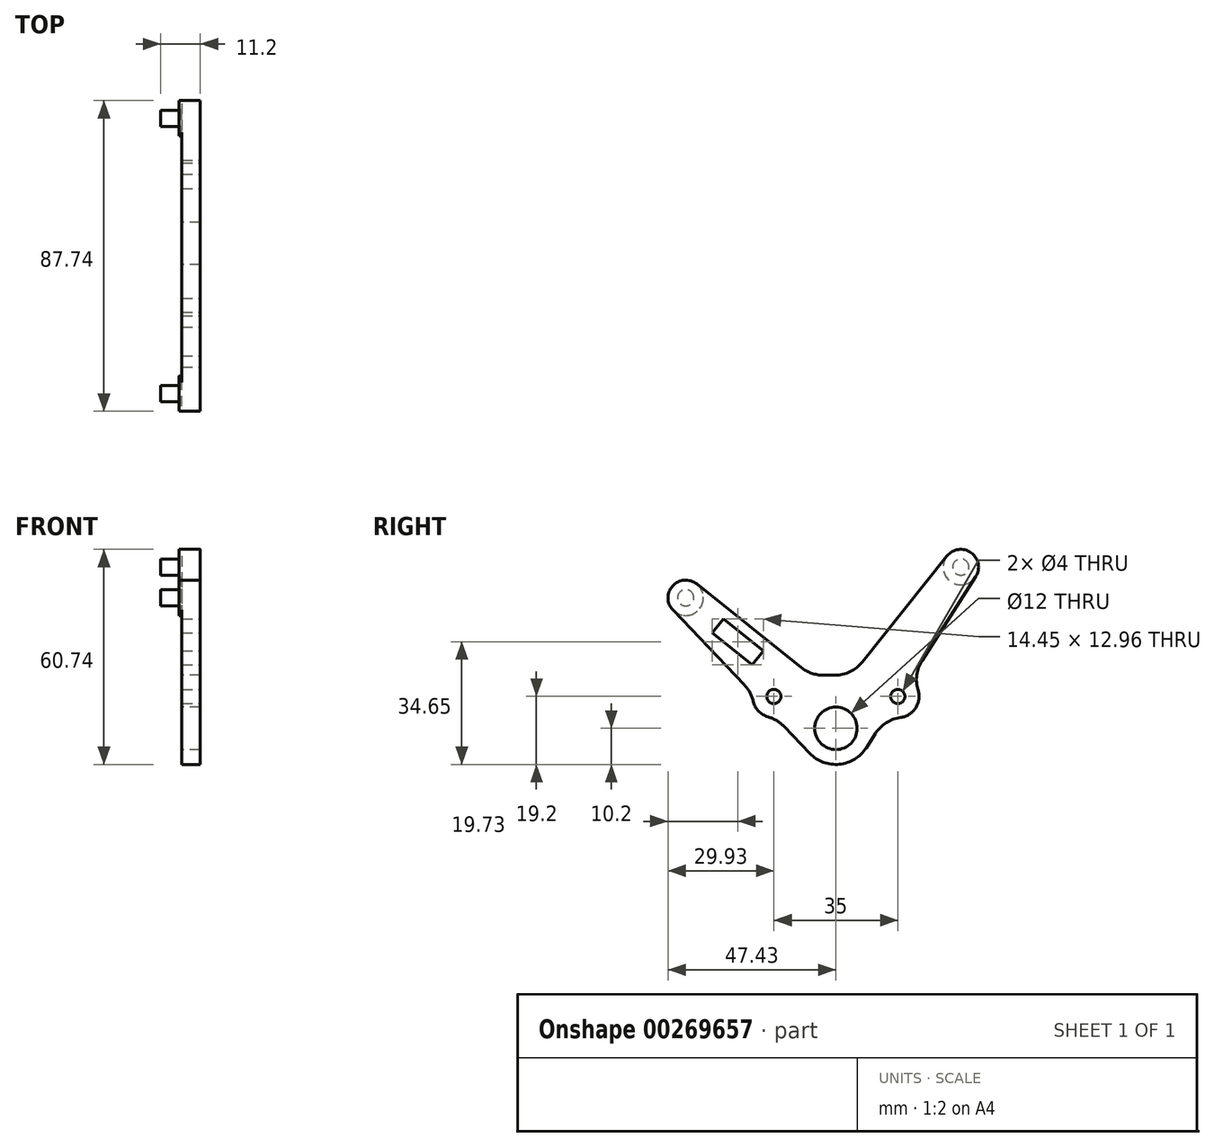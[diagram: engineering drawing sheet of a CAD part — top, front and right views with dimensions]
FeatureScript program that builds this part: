
annotation { "Feature Type Name" : "Feature", "Feature Type Description" : "" }
export const myFeature = defineFeature(function(context is Context, id is Id, definition is map)
    precondition{}
    {
        {
            var Q0;
            Q0=qCreatedBy(makeId("Right.planeOp"),FACE);
            var sketch = newSketch(context, id + "F0", { "sketchPlane" : qUnion([Q0])});
            skArc(sketch, "E0", {"start": v(-7.37, -7.05) * mm, "mid": v(0.99, -10.15) * mm, "end": v(8.6, -5.5) * mm});
            skLineSegment(sketch, "E1", {"start": v(39.52, 42.85) * mm, "end": v(8.6, -5.5) * mm});
            skLineSegment(sketch, "E2", {"start": v(-46.04, 33.4) * mm, "end": v(-7.37, -7.05) * mm});
            skCircle(sketch, "E3", {"center": v(0, 0) * mm, "radius": 6 * mm});
            skLineSegment(sketch, "E4", {"start": v(31.4, 48.66) * mm, "end": v(0, 9.36) * mm});
            skLineSegment(sketch, "E5", {"start": v(0, 9.36) * mm, "end": v(-39.3, 40.76) * mm});
            skArc(sketch, "E6", {"start": v(39.52, 42.85) * mm, "mid": v(38.22, 49.6) * mm, "end": v(31.4, 48.66) * mm});
            skArc(sketch, "E7", {"start": v(-39.3, 40.76) * mm, "mid": v(-46.12, 40.23) * mm, "end": v(-46.04, 33.4) * mm});
            skLineSegment(sketch, "E8", {"start": v(35.31, 45.54) * mm, "end": v(-42.43, 36.86) * mm, "construction": true});
            skSolve(sketch);
        }
        {
            var Q0;
            Q0 = qSketchRegion(id + "F0", true);
            extrude(context, id + "F1", {"entities" : qUnion([Q0]), "depth" : 5.2 * mm});
        }
        {
            var Q0;
            Q0=makeQuery(id+"F1.opExtrude","CAP_FACE",FACE,{"disambiguationData":[OSD([sQuery(id+"F0.wireOp",EDGE,"E0"),sQuery(id+"F0.wireOp",EDGE,"E1"),sQuery(id+"F0.wireOp",EDGE,"E2"),sQuery(id+"F0.wireOp",EDGE,"E3"),sQuery(id+"F0.wireOp",EDGE,"6CrYnnp3-bjRy-a3A9-He7e-rV40i75ghI31.top"),sQuery(id+"F0.wireOp",EDGE,"6CrYnnp3-bjRy-a3A9-He7e-rV40i75ghI31.left"),sQuery(id+"F0.wireOp",EDGE,"6CrYnnp3-bjRy-a3A9-He7e-rV40i75ghI31.right")])],"isStart":false});
            var sketch = newSketch(context, id + "F2", { "sketchPlane" : qUnion([Q0])});
            skLineSegment(sketch, "E9", {"start": v(17.5, 3) * mm, "end": v(5.2, 3) * mm});
            skArc(sketch, "E10", {"start": v(17.5, 3) * mm, "mid": v(23.5, 9) * mm, "end": v(17.5, 15) * mm});
            skLineSegment(sketch, "E11", {"start": v(0, 0) * mm, "end": v(0, 22.38) * mm, "construction": true});
            skLineSegment(sketch, "E12.trimOffspring", {"start": v(-5.2, 3) * mm, "end": v(-17.5, 3) * mm});
            skLineSegment(sketch, "E13", {"start": v(17.5, 9) * mm, "end": v(-17.5, 9) * mm, "construction": true});
            skArc(sketch, "E14.0", {"start": v(5.2, 3) * mm, "mid": v(0, 6) * mm, "end": v(-5.2, 3) * mm});
            skArc(sketch, "E15", {"start": v(-17.5, 15) * mm, "mid": v(-23.5, 9) * mm, "end": v(-17.5, 3) * mm});
            skLineSegment(sketch, "E16", {"start": v(17.5, 15) * mm, "end": v(-17.5, 15) * mm});
            skSolve(sketch);
        }
        {
            var Q0;
            Q0 = qSketchRegion(id + "F2", true);
            var Q1;
            Q1=makeQuery(id+"F1.opExtrude","CAP_FACE",FACE,{"disambiguationData":[OSD([sQuery(id+"F0.wireOp",EDGE,"E0"),sQuery(id+"F0.wireOp",EDGE,"E1"),sQuery(id+"F0.wireOp",EDGE,"E2"),sQuery(id+"F0.wireOp",EDGE,"E3"),sQuery(id+"F0.wireOp",EDGE,"6CrYnnp3-bjRy-a3A9-He7e-rV40i75ghI31.top"),sQuery(id+"F0.wireOp",EDGE,"6CrYnnp3-bjRy-a3A9-He7e-rV40i75ghI31.left"),sQuery(id+"F0.wireOp",EDGE,"6CrYnnp3-bjRy-a3A9-He7e-rV40i75ghI31.right")])],"isStart":true});
            extrude(context, id + "F3", {"entities" : qUnion([Q0]), "operationType" : NewBodyOperationType.ADD, "endBound" : BoundingType.UP_TO_SURFACE, "oppositeDirection" : true, "endBoundEntityFace" : qUnion([Q1]), "depth" : 25 * mm});
        }
        {
            var Q0;
            Q0=makeQuery(id+"F3.boolean.opBoolean","MERGE",FACE,{"derivedFrom":[makeQuery(id+"F1.opExtrude","CAP_FACE",FACE,{"disambiguationData":[OSD([sQuery(id+"F0.wireOp",EDGE,"E0"),sQuery(id+"F0.wireOp",EDGE,"E1"),sQuery(id+"F0.wireOp",EDGE,"E2"),sQuery(id+"F0.wireOp",EDGE,"E3"),sQuery(id+"F0.wireOp",EDGE,"6CrYnnp3-bjRy-a3A9-He7e-rV40i75ghI31.top"),sQuery(id+"F0.wireOp",EDGE,"6CrYnnp3-bjRy-a3A9-He7e-rV40i75ghI31.left"),sQuery(id+"F0.wireOp",EDGE,"6CrYnnp3-bjRy-a3A9-He7e-rV40i75ghI31.right")])],"isStart":false}),makeQuery(id+"F3.opExtrude","CAP_FACE",FACE,{"disambiguationData":[OSD([sQuery(id+"F2.wireOp",EDGE,"E9"),sQuery(id+"F2.wireOp",EDGE,"E10"),sQuery(id+"F2.wireOp",EDGE,"EYINIPp3-QXVF-pmR1-TqJy-1Ml2RVj9I1TC")])],"isStart":true}),makeQuery(id+"F3.opExtrude","CAP_FACE",FACE,{"disambiguationData":[OSD([sQuery(id+"F2.wireOp",EDGE,"iWNl47SU-lmgI-QhfJ-MTGu-GNKagXJEW7x7"),sQuery(id+"F2.wireOp",EDGE,"ciIXBD7B-xHR2-47Qe-O2mZ-nUJdmOusYSC5"),sQuery(id+"F2.wireOp",EDGE,"E12.trimOffspring")])],"isStart":true})]});
            var sketch = newSketch(context, id + "F4", { "sketchPlane" : qUnion([Q0])});
            skLineSegment(sketch, "E17", {"start": v(-17.5, 9) * mm, "end": v(17.5, 9) * mm, "construction": true});
            skLineSegment(sketch, "E18", {"start": v(0, 0.97) * mm, "end": v(0, 29.51) * mm, "construction": true});
            skCircle(sketch, "E19", {"center": v(-17.5, 9) * mm, "radius": 2 * mm});
            skCircle(sketch, "E20", {"center": v(17.5, 9) * mm, "radius": 2 * mm});
            skSolve(sketch);
        }
        {
            var Q0;
            Q0 = qSketchRegion(id + "F4", true);
            extrude(context, id + "F5", {"entities" : qUnion([Q0]), "operationType" : NewBodyOperationType.REMOVE, "endBound" : BoundingType.THROUGH_ALL, "oppositeDirection" : true, "depth" : 25 * mm});
        }
        {
            var Q0;
            {var subQ0=sQuery(id+"F0.wireOp",EDGE,"E7");var subQ1=sQuery(id+"F0.wireOp",EDGE,"E6");var subQ2=sQuery(id+"F0.wireOp",EDGE,"E5");var subQ3=sQuery(id+"F0.wireOp",EDGE,"E4");var subQ4=sQuery(id+"F0.wireOp",EDGE,"E3");var subQ5=sQuery(id+"F0.wireOp",EDGE,"E2");var subQ6=sQuery(id+"F0.wireOp",EDGE,"E1");var subQ7=sQuery(id+"F0.wireOp",EDGE,"E0");Q0=makeQuery(id+"F3.boolean.opBoolean","MERGE",FACE,{"derivedFrom":[makeQuery(id+"F1.opExtrude","CAP_FACE",FACE,{"disambiguationData":[OSD([subQ7,subQ6,subQ5,subQ4,subQ3,subQ2,subQ1,subQ0])],"isStart":true}),makeQuery(id+"F3.opExtrude","CAP_FACE",FACE,{"disambiguationData":[OSD([subQ7,subQ6,subQ5,subQ4,subQ3,subQ2,subQ1,subQ0]),ownerDisambiguation([makeQuery(id+"F3.opExtrude","SWEPT_BODY",BODY,{"disambiguationData":[OSD([sQuery(id+"F2.wireOp",EDGE,"E9"),sQuery(id+"F2.wireOp",EDGE,"E10"),sQuery(id+"F2.wireOp",EDGE,"EYINIPp3-QXVF-pmR1-TqJy-1Ml2RVj9I1TC")])]})])],"isStart":false}),makeQuery(id+"F3.opExtrude","CAP_FACE",FACE,{"disambiguationData":[OSD([subQ7,subQ6,subQ5,subQ4,subQ3,subQ2,subQ1,subQ0]),ownerDisambiguation([makeQuery(id+"F3.opExtrude","SWEPT_BODY",BODY,{"disambiguationData":[OSD([sQuery(id+"F2.wireOp",EDGE,"iWNl47SU-lmgI-QhfJ-MTGu-GNKagXJEW7x7"),sQuery(id+"F2.wireOp",EDGE,"ciIXBD7B-xHR2-47Qe-O2mZ-nUJdmOusYSC5"),sQuery(id+"F2.wireOp",EDGE,"E12.trimOffspring")])]})])],"isStart":false})]});}
            var sketch = newSketch(context, id + "F6", { "sketchPlane" : qUnion([Q0])});
            skCircle(sketch, "E21", {"center": v(-35.31, 45.54) * mm, "radius": 2.3 * mm});
            skCircle(sketch, "E22", {"center": v(42.43, 36.86) * mm, "radius": 2.3 * mm});
            skSolve(sketch);
        }
        {
            var Q0;
            Q0 = qSketchRegion(id + "F6", true);
            extrude(context, id + "F7", {"entities" : qUnion([Q0]), "operationType" : NewBodyOperationType.ADD, "depth" : 6 * mm});
        }
        {
            var Q0;
            Q0=makeQuery(id+"F3.boolean.opBoolean","INTERSECT",EDGE,{"derivedFrom":[makeQuery(id+"F1.opExtrude","SWEPT_FACE",FACE,{"disambiguationData":[OSD([sQuery(id+"F0.wireOp",EDGE,"E4")])]}),makeQuery(id+"F3.opExtrude","SWEPT_FACE",FACE,{"disambiguationData":[OSD([sQuery(id+"F2.wireOp",EDGE,"E16")])]})]});
            var Q1;
            Q1=makeQuery(id+"F3.boolean.opBoolean","INTERSECT",EDGE,{"derivedFrom":[makeQuery(id+"F1.opExtrude","SWEPT_FACE",FACE,{"disambiguationData":[OSD([sQuery(id+"F0.wireOp",EDGE,"E5")])]}),makeQuery(id+"F3.opExtrude","SWEPT_FACE",FACE,{"disambiguationData":[OSD([sQuery(id+"F2.wireOp",EDGE,"E16")])]})]});
            var Q2;
            Q2=makeQuery(id+"F3.boolean.opBoolean","INTERSECT",EDGE,{"derivedFrom":[makeQuery(id+"F1.opExtrude","SWEPT_FACE",FACE,{"disambiguationData":[OSD([sQuery(id+"F0.wireOp",EDGE,"E1")])]}),makeQuery(id+"F3.opExtrude","SWEPT_FACE",FACE,{"disambiguationData":[OSD([sQuery(id+"F2.wireOp",EDGE,"E10")])]})]});
            var Q3;
            Q3=makeQuery(id+"F3.boolean.opBoolean","INTERSECT",EDGE,{"derivedFrom":[makeQuery(id+"F1.opExtrude","SWEPT_FACE",FACE,{"disambiguationData":[OSD([sQuery(id+"F0.wireOp",EDGE,"E1")])]}),makeQuery(id+"F3.opExtrude","SWEPT_FACE",FACE,{"disambiguationData":[OSD([sQuery(id+"F2.wireOp",EDGE,"E9")])]})]});
            var Q4;
            Q4=makeQuery(id+"F3.boolean.opBoolean","INTERSECT",EDGE,{"derivedFrom":[makeQuery(id+"F1.opExtrude","SWEPT_FACE",FACE,{"disambiguationData":[OSD([sQuery(id+"F0.wireOp",EDGE,"E2")])]}),makeQuery(id+"F3.opExtrude","SWEPT_FACE",FACE,{"disambiguationData":[OSD([sQuery(id+"F2.wireOp",EDGE,"E12.trimOffspring")])]})]});
            var Q5;
            Q5=makeQuery(id+"F3.boolean.opBoolean","INTERSECT",EDGE,{"derivedFrom":[makeQuery(id+"F1.opExtrude","SWEPT_FACE",FACE,{"disambiguationData":[OSD([sQuery(id+"F0.wireOp",EDGE,"E2")])]}),makeQuery(id+"F3.opExtrude","SWEPT_FACE",FACE,{"disambiguationData":[OSD([sQuery(id+"F2.wireOp",EDGE,"E15")])]})]});
            fillet(context, id + "F8", {"entities" : qUnion([Q0, Q1, Q2, Q3, Q4, Q5]), "radius" : 10 * mm, "tangentPropagation" : true, "allowEdgeOverflow" : false});
        }
        {
            var Q0;
            {var subQ0=sQuery(id+"F0.wireOp",EDGE,"E7");var subQ1=sQuery(id+"F0.wireOp",EDGE,"E6");var subQ2=sQuery(id+"F0.wireOp",EDGE,"E5");var subQ3=sQuery(id+"F0.wireOp",EDGE,"E4");var subQ4=sQuery(id+"F0.wireOp",EDGE,"E3");var subQ5=sQuery(id+"F0.wireOp",EDGE,"E2");var subQ6=sQuery(id+"F0.wireOp",EDGE,"E1");var subQ7=sQuery(id+"F0.wireOp",EDGE,"E0");Q0=makeQuery(id+"F3.boolean.opBoolean","MERGE",FACE,{"derivedFrom":[makeQuery(id+"F1.opExtrude","CAP_FACE",FACE,{"disambiguationData":[OSD([subQ7,subQ6,subQ5,subQ4,subQ3,subQ2,subQ1,subQ0])],"isStart":true}),makeQuery(id+"F3.opExtrude","CAP_FACE",FACE,{"disambiguationData":[OSD([subQ7,subQ6,subQ5,subQ4,subQ3,subQ2,subQ1,subQ0])],"isStart":false})]});}
            var sketch = newSketch(context, id + "F9", { "sketchPlane" : qUnion([Q0])});
            skCircle(sketch, "E23", {"center": v(-35.31, 45.54) * mm, "radius": 5 * mm});
            skCircle(sketch, "E24", {"center": v(42.43, 36.86) * mm, "radius": 5 * mm});
            skSolve(sketch);
        }
        {
            var Q0;
            Q0 = qSketchRegion(id + "F9", true);
            extrude(context, id + "F10", {"entities" : qUnion([Q0]), "operationType" : NewBodyOperationType.ADD, "depth" : .8 * mm});
        }
        {
            var Q0;
            Q0=makeQuery(id+"F3.boolean.opBoolean","MERGE",FACE,{"derivedFrom":[makeQuery(id+"F1.opExtrude","CAP_FACE",FACE,{"disambiguationData":[OSD([sQuery(id+"F0.wireOp",EDGE,"E0"),sQuery(id+"F0.wireOp",EDGE,"E1"),sQuery(id+"F0.wireOp",EDGE,"E2"),sQuery(id+"F0.wireOp",EDGE,"E3"),sQuery(id+"F0.wireOp",EDGE,"E4"),sQuery(id+"F0.wireOp",EDGE,"E5"),sQuery(id+"F0.wireOp",EDGE,"E6"),sQuery(id+"F0.wireOp",EDGE,"E7")])],"isStart":false}),makeQuery(id+"F3.opExtrude","CAP_FACE",FACE,{"disambiguationData":[OSD([sQuery(id+"F2.wireOp",EDGE,"E9"),sQuery(id+"F2.wireOp",EDGE,"E10"),sQuery(id+"F2.wireOp",EDGE,"E12.trimOffspring"),sQuery(id+"F2.wireOp",EDGE,"E14.0"),sQuery(id+"F2.wireOp",EDGE,"E15"),sQuery(id+"F2.wireOp",EDGE,"E16")])],"isStart":true})]});
            var sketch = newSketch(context, id + "F11", { "sketchPlane" : qUnion([Q0])});
            skLineSegment(sketch, "E25", {"start": v(-31.8, 30.93) * mm, "end": v(-20.48, 21.88) * mm});
            skLineSegment(sketch, "E26", {"start": v(-20.48, 21.88) * mm, "end": v(-23.6, 17.97) * mm});
            skLineSegment(sketch, "E27", {"start": v(-23.6, 17.97) * mm, "end": v(-34.92, 27.02) * mm});
            skLineSegment(sketch, "E28", {"start": v(-34.92, 27.02) * mm, "end": v(-31.8, 30.93) * mm});
            skSolve(sketch);
        }
        {
            var Q0;
            Q0 = qSketchRegion(id + "F11", true);
            extrude(context, id + "F12", {"entities" : qUnion([Q0]), "operationType" : NewBodyOperationType.REMOVE, "endBound" : BoundingType.THROUGH_ALL, "oppositeDirection" : true, "depth" : 25 * mm});
        }
    });
